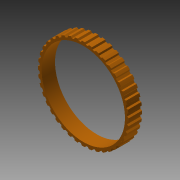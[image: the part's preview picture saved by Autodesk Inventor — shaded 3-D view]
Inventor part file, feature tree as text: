
AUTODESK INVENTOR PART (.ipt)
format: ipt  version: 2013 (Build 170138000, 138)  size: 272,384 bytes
history: native  units: in
note: dims shown in document units (in); Inventor stores cm internally (conversion verified against a paired STEP export)
features: extrude x1, sketch x1
ambient origin geometry x8: Origin, YZ Plane, XZ Plane, XY Plane, X Axis, Y Axis, Z Axis, Center Point
bodies: Solid1 (feature_tree)
feature tree (2):
  extrude  "Extrusion1"  Depth=5.6in
  sketch  "Sketch1"  dims[d0=0.9in d1=0.0in d2=5.6in]
